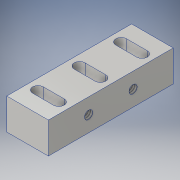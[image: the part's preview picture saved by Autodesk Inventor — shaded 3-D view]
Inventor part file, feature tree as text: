
AUTODESK INVENTOR PART (.ipt)
format: ipt  version: 2016 (Build 200138000, 138)  size: 139,264 bytes
history: native  units: in
note: dims shown in document units (in); Inventor stores cm internally (conversion verified against a paired STEP export)
features: sketch x3, extrude x2, hole x1
ambient origin geometry x8: Origin, YZ Plane, XZ Plane, XY Plane, X Axis, Y Axis, Z Axis, Center Point
bodies: Solid1 (feature_tree)
feature tree (6):
  extrude  "Stock Bar"  Depth=0.75in
  hole  "Motor Support Mounting Holes"  [1 undecoded]
  extrude  "Table Mounting Slots"  Depth=1.0in
  sketch  "Sketch1"  dims[d0=1.0in d1=0.75in]
  sketch  "Sketch2"  dims[d2=3.0in d3=0.0in d4=1.068in]
  sketch  "Sketch3"  dims[d6=0.375in d7=0.375in d8=0.196in d9=0.875in d10=0.375in d11=0.25in d12=0.5635in d13=0.875in d14=0.8108in d15=0.13in d16=0.13in d17=0.13in d18=0.5in d19=0.5in d20=0.5in d21=1.0in d22=1.0in d23=0.25in d24=0.25in d25=0.25in d26=0.5in d27=4.0in d28=0.0in d29=0.966in]
note: 1 required parameter value undecoded (feature->parameter linkage not recoverable at this tier; creation-order binding heuristic only, values carry confidence <= 0.55)
